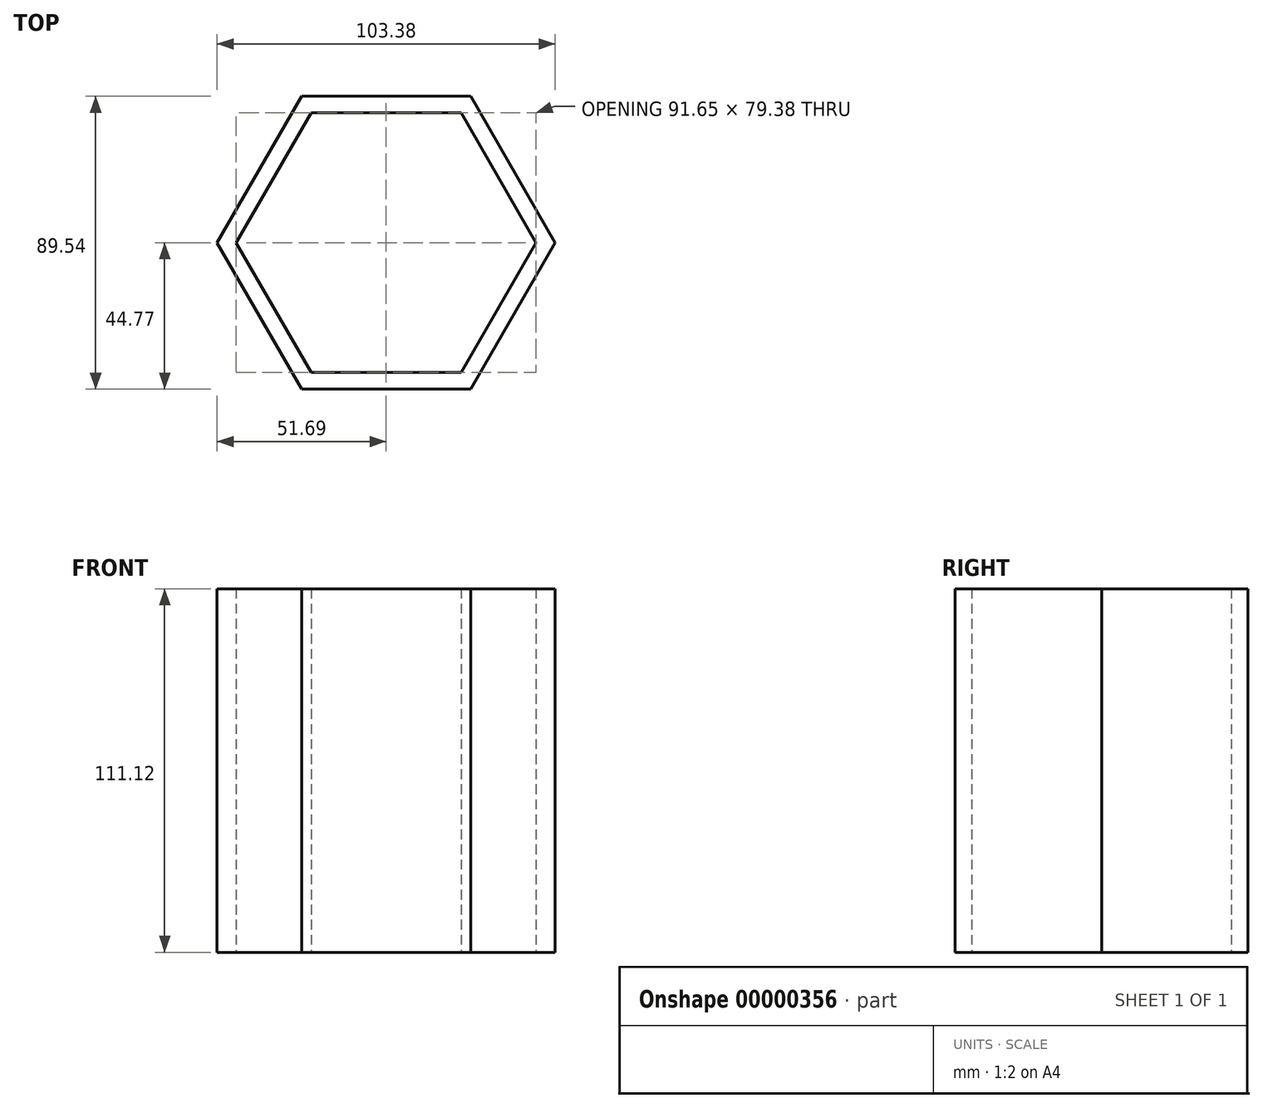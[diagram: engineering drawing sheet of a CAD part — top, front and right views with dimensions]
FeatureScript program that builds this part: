
annotation { "Feature Type Name" : "Feature", "Feature Type Description" : "" }
export const myFeature = defineFeature(function(context is Context, id is Id, definition is map)
    precondition{}
    {
        {
            var Q0;
            Q0=qCreatedBy(makeId("Top.planeOp"),FACE);
            var sketch = newSketch(context, id + "F0", { "sketchPlane" : qUnion([Q0])});
            skLineSegment(sketch, "E0.rect.bottom", {"start": v(-44.45, 44.45) * mm, "end": v(44.45, 44.45) * mm, "construction": true});
            skLineSegment(sketch, "E0.rect.top", {"start": v(-44.45, -44.45) * mm, "end": v(44.45, -44.45) * mm, "construction": true});
            skLineSegment(sketch, "E0.rect.left", {"start": v(-44.45, 44.45) * mm, "end": v(-44.45, -44.45) * mm, "construction": true});
            skLineSegment(sketch, "E0.rect.right", {"start": v(44.45, 44.45) * mm, "end": v(44.45, -44.45) * mm, "construction": true});
            skPoint(sketch, "E0.rect.middle", {"position": v(0, 0) * mm});
            skLineSegment(sketch, "E1", {"start": v(-45.83, 0) * mm, "end": v(-22.91, 39.69) * mm});
            skLineSegment(sketch, "E2", {"start": v(-22.91, 39.69) * mm, "end": v(22.91, 39.69) * mm});
            skLineSegment(sketch, "E3", {"start": v(22.91, 39.69) * mm, "end": v(45.83, 0) * mm});
            skLineSegment(sketch, "E4", {"start": v(45.83, 0) * mm, "end": v(22.91, -39.69) * mm});
            skLineSegment(sketch, "E5", {"start": v(22.91, -39.69) * mm, "end": v(-22.91, -39.69) * mm});
            skLineSegment(sketch, "E6", {"start": v(-22.91, -39.69) * mm, "end": v(-45.83, 0) * mm});
            skLineSegment(sketch, "E7", {"start": v(-22.91, 39.69) * mm, "end": v(22.91, -39.69) * mm, "construction": true});
            skLineSegment(sketch, "E8", {"start": v(22.91, 39.69) * mm, "end": v(-22.91, -39.69) * mm, "construction": true});
            skLineSegment(sketch, "E9", {"start": v(-45.83, 0) * mm, "end": v(45.83, 0) * mm, "construction": true});
            skLineSegment(sketch, "E10.0", {"start": v(-51.7, 0) * mm, "end": v(-25.85, 44.77) * mm});
            skLineSegment(sketch, "E10.1", {"start": v(-25.85, -44.77) * mm, "end": v(-51.7, 0) * mm});
            skLineSegment(sketch, "E10.2", {"start": v(25.85, -44.77) * mm, "end": v(-25.85, -44.77) * mm});
            skLineSegment(sketch, "E10.3", {"start": v(51.7, 0) * mm, "end": v(25.85, -44.77) * mm});
            skLineSegment(sketch, "E10.4", {"start": v(25.85, 44.77) * mm, "end": v(51.7, 0) * mm});
            skLineSegment(sketch, "E10.5", {"start": v(-25.85, 44.77) * mm, "end": v(25.85, 44.77) * mm});
            skSolve(sketch);
        }
        {
            var Q0;
            Q0=makeQuery(id+"F0.imprint","IMPRINT",FACE,{"disambiguationData":[TD([[makeQuery(id+"F0.imprint","IMPRINT",EDGE,{"derivedFrom":sQuery(id+"F0.wireOp",EDGE,"E1")}),1.0]])]});
            extrude(context, id + "F1", {"entities" : qUnion([Q0]), "depth" : 111.12 * mm});
        }
    });
